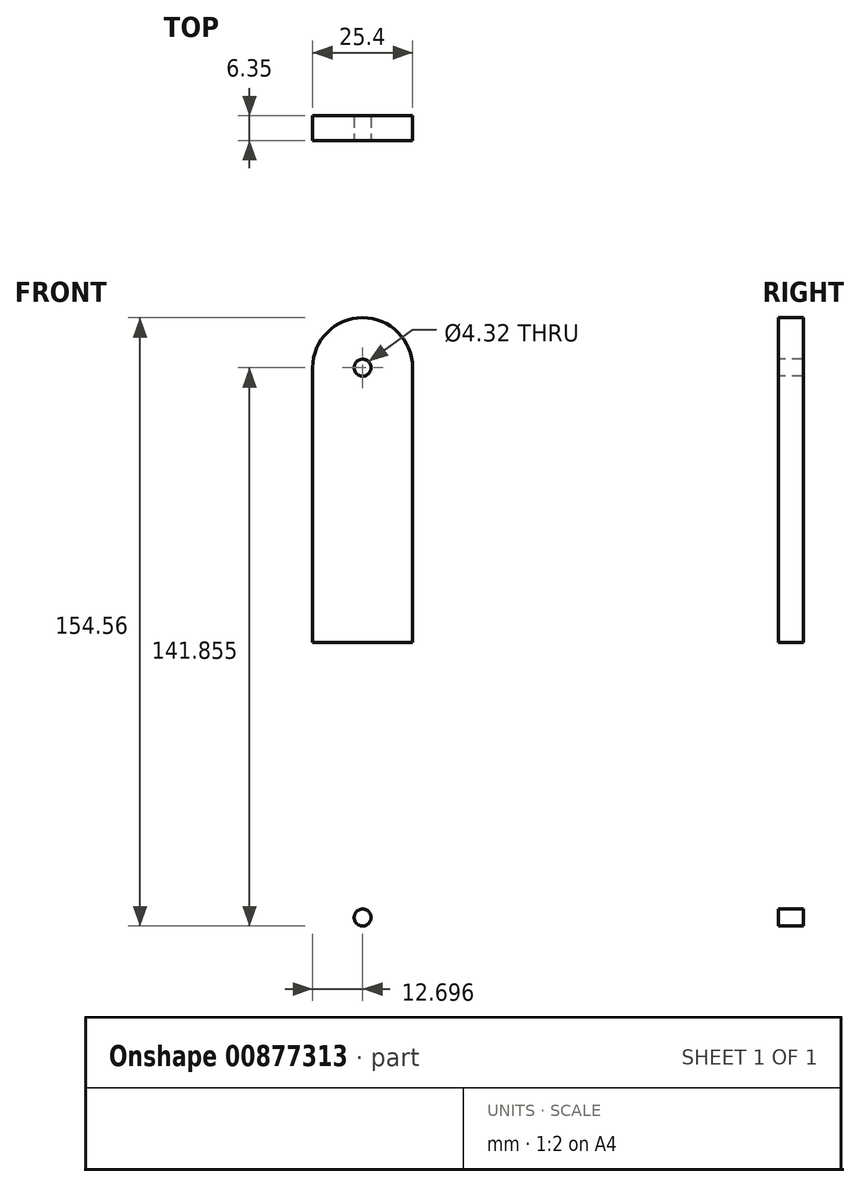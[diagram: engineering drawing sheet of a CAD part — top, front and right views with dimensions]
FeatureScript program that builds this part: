
annotation { "Feature Type Name" : "Feature", "Feature Type Description" : "" }
export const myFeature = defineFeature(function(context is Context, id is Id, definition is map)
    precondition{}
    {
        {
            var Q0;
            Q0=qCreatedBy(makeId("Front.planeOp"),FACE);
            var sketch = newSketch(context, id + "F0", { "sketchPlane" : qUnion([Q0])});
            skLineSegment(sketch, "E0.bottom", {"start": v(-137.16, 110.5) * mm, "end": v(-111.76, 110.5) * mm});
            skLineSegment(sketch, "E0.top", {"start": v(-137.16, -54.6) * mm, "end": v(-111.76, -54.6) * mm});
            skLineSegment(sketch, "E0.left", {"start": v(-137.16, 110.5) * mm, "end": v(-137.16, -54.6) * mm});
            skLineSegment(sketch, "E0.right", {"start": v(-111.76, 110.5) * mm, "end": v(-111.76, -54.6) * mm});
            skSolve(sketch);
        }
        {
            var Q0;
            Q0=makeQuery(id+"F0.imprint","IMPRINT",FACE,{"disambiguationData":[TD([[makeQuery(id+"F0.imprint","IMPRINT",EDGE,{"derivedFrom":sQuery(id+"F0.wireOp",EDGE,"E0.bottom")}),-1.0]])]});
            extrude(context, id + "F1", {"entities" : qUnion([Q0]), "depth" : 6.35 * mm, "offsetDistance" : 25.4 * mm});
        }
        {
            var Q0;
            Q0=makeQuery(id+"F1.opExtrude","CAP_FACE",FACE,{"disambiguationData":[OSD([sQuery(id+"F0.wireOp",EDGE,"E0.bottom"),sQuery(id+"F0.wireOp",EDGE,"E0.top"),sQuery(id+"F0.wireOp",EDGE,"E0.left"),sQuery(id+"F0.wireOp",EDGE,"E0.right")])],"isStart":false});
            var sketch = newSketch(context, id + "F2", { "sketchPlane" : qUnion([Q0])});
            skCircle(sketch, "E1", {"center": v(-124.46, 97.8) * mm, "radius": 2.16 * mm});
            skLineSegment(sketch, "E2", {"start": v(-137.16, 27.96) * mm, "end": v(-111.76, 27.96) * mm});
            skCircle(sketch, "E3.MirrorC", {"center": v(-124.46, -41.9) * mm, "radius": 2.16 * mm});
            skSolve(sketch);
        }
        {
            var Q0;
            Q0=makeQuery(id+"F2.imprint","IMPRINT",FACE,{"disambiguationData":[TD([[makeQuery(id+"F2.imprint","IMPRINT",EDGE,{"derivedFrom":sQuery(id+"F2.wireOp",EDGE,"E1")}),1.0]])]});
            var Q1;
            Q1=makeQuery(id+"F2.imprint","IMPRINT",FACE,{"disambiguationData":[TD([[makeQuery(id+"F2.imprint","IMPRINT",EDGE,{"derivedFrom":sQuery(id+"F2.wireOp",EDGE,"E3.MirrorC")}),-1.0]])]});
            extrude(context, id + "F3", {"entities" : qUnion([Q0, Q1]), "operationType" : NewBodyOperationType.REMOVE, "oppositeDirection" : true, "depth" : 25.4 * mm, "offsetDistance" : 25.4 * mm});
        }
        {
            var Q0;
            Q0=makeQuery(id+"F1.opExtrude","SWEPT_EDGE",EDGE,{"disambiguationData":[OSD([sQuery(id+"F0.wireOp",EDGE,"E0.bottom"),sQuery(id+"F0.wireOp",EDGE,"E0.left")])]});
            var Q1;
            Q1=makeQuery(id+"F1.opExtrude","SWEPT_EDGE",EDGE,{"disambiguationData":[OSD([sQuery(id+"F0.wireOp",EDGE,"E0.bottom"),sQuery(id+"F0.wireOp",EDGE,"E0.right")])]});
            var Q2;
            Q2=makeQuery(id+"F1.opExtrude","SWEPT_EDGE",EDGE,{"disambiguationData":[OSD([sQuery(id+"F0.wireOp",EDGE,"E0.top"),sQuery(id+"F0.wireOp",EDGE,"E0.left")])]});
            var Q3;
            Q3=makeQuery(id+"F1.opExtrude","SWEPT_EDGE",EDGE,{"disambiguationData":[OSD([sQuery(id+"F0.wireOp",EDGE,"E0.top"),sQuery(id+"F0.wireOp",EDGE,"E0.right")])]});
            fillet(context, id + "F4", {"entities" : qUnion([Q0, Q1, Q2, Q3]), "radius" : 12.7 * mm, "tangentPropagation" : true, "allowEdgeOverflow" : false});
        }
    });
